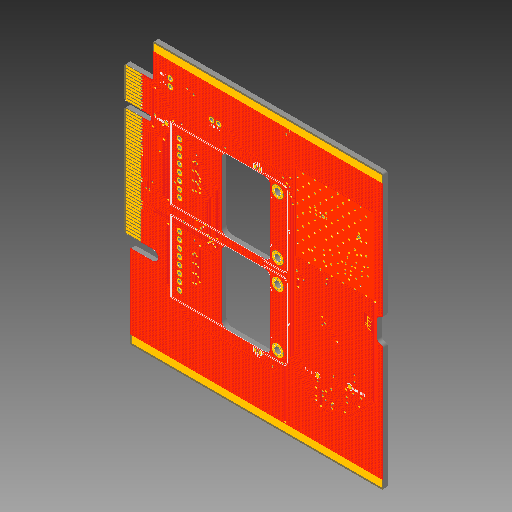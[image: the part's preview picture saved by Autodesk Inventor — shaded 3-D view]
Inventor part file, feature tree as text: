
AUTODESK INVENTOR PART (.ipt)
format: ipt  version: 2018 (Build 220112000, 112)  size: 1,708,544 bytes
history: native  units: in
note: dims shown in document units (in); Inventor stores cm internally (conversion verified against a paired STEP export)
features: sketch x9, hole x5, other x4, extrude x2, projected_geometry x2, chamfer x1, fillet x1
ambient origin geometry x8: Origin, YZ Plane, XZ Plane, XY Plane, X Axis, Y Axis, Z Axis, Center Point
bodies: Solid1 (feature_tree)
feature tree (24):
  extrude  "Extrusion1"  Depth=3.7717in
  chamfer  "Chamfer1"  Distance=0.063in
  fillet  "Fillet1"  Radius=3.7795in
  extrude  "Extrusion6"  Depth=0.0039in
  other  "Decal4"
  other  "Decal5"
  hole  "Hole9"  [1 undecoded]
  hole  "Hole10"  [1 undecoded]
  hole  "Hole11"  [1 undecoded]
  hole  "Hole12"  [1 undecoded]
  hole  "Hole13"  [1 undecoded]
  sketch  "Sketch26"  dims[d37=0.5709in d38=0.0453in d39=0.0709in d40=2.7559in d42=0.0709in d43=1.9685in d45=0.0709in d48=0.0787in d49=0.1339in d50=0.0748in d51=0.3307in d52=0.9449in d53=0.0197in d54=0.0787in d55=45.0deg d56=0.0197in d145=0.2362in d146=0.0394in d147=0.1181in d148=0.0591in d149=1.3406in d150=2.0098in d151=1.0433in d152=0.0787in d153=0.3937in d154=0.0in d162=0.0866in d163=0.2362in d164=0.1575in d165=0.0787in d166=90.0deg d167=0.315in d168=0.8108in d169=0.0394in d170=0.2362in d171=0.1575in d172=0.0787in d173=90.0deg d174=0.315in d175=0.8108in d176=0.0236in d177=0.2362in d178=0.1575in d179=0.0787in d180=90.0deg d181=0.315in d182=0.8108in d183=0.0138in d184=0.2362in d185=0.1575in d186=0.0787in d187=90.0deg d188=0.315in d189=0.8108in d190=0.0118in d191=0.2362in d192=0.1575in d193=0.0787in d194=90.0deg d195=0.315in d196=0.8108in d205=0.0197in d206=0.1181in d207=9.8425in d209=0.0394in d210=0.7874in d212=0.0394in]
  sketch  "Sketch16"  dims[d0=2.0197in d1=3.7717in]
  projected_geometry  "Projected Loop5"
  sketch  "Sketch19"  dims[d3=0.3937in d4=0.063in d5=0.0in d20=3.7795in]
  sketch  "Sketch20"  dims[d21=3.7795in d22=0.0039in]
  sketch  "Sketch21"  dims[d23=0.0039in d24=0.0787in]
  sketch  "Sketch22"  dims[d25=0.0039in d28=0.4429in]
  sketch  "Sketch23"  dims[d29=2.2047in d31=0.374in]
  sketch  "Sketch24"  dims[d32=1.2008in d34=0.1378in]
  sketch  "Sketch25"  dims[d35=0.4783in d36=1.5413in]
  other  "Image9"
  other  "Image10"
  projected_geometry  "Projected Loop6"
note: 5 required parameter values undecoded (feature->parameter linkage not recoverable at this tier; creation-order binding heuristic only, values carry confidence <= 0.55)
